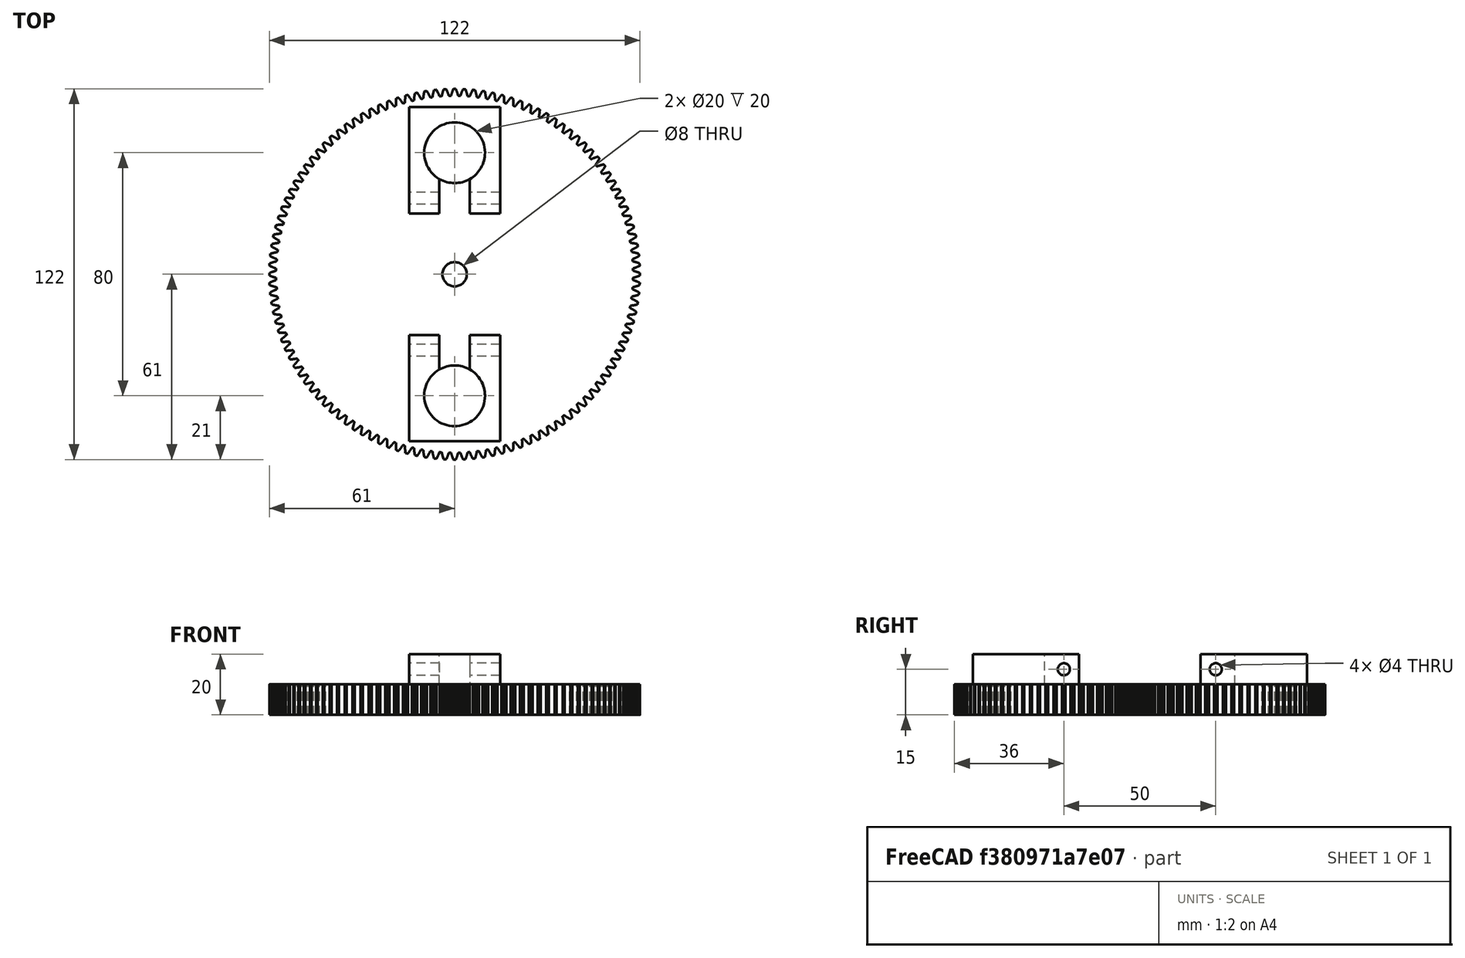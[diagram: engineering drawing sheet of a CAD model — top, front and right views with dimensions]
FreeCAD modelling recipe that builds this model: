
FCSTD DOCUMENT  (FreeCAD 0.17R13522 (Git))
Label: cogwheel-swivel
License: All rights reserved
LicenseURL: http://en.wikipedia.org/wiki/All_rights_reserved
objects: Part::Cylinder×5, Part::Box×3, Part::MultiFuse×2, Part::FeaturePython×1, Part::Cut×1
note: 12 computed .brp shape members not serialized (recipe doc carries the construction recipe); baked Part::Feature solids carry a one-line shape summary decoded from their .brp

FEATURE [Part::FeaturePython] InvoluteGear  # WARN: FeaturePython — macro-defined, semantics opaque (R4)
  backlash = 0
  beta = 0
  clearance = 0.25
  double_helix = false
  head = 0
  height = 10
  module = 1
  numpoints = 6
  pressure_angle = 20
  reversed_backlash = false
  shift = 0
  simple = false
  teeth = 120
  undercut = false
FEATURE [Part::Cylinder] Cylinder
  Angle = 360
  AttacherType = Attacher::AttachEngine3D
  Height = 20
  Placement = pos=(0,-40,0) rot=(0,0,1;0rad)
  Radius = 10
FEATURE [Part::Cylinder] Cylinder001
  Angle = 360
  AttacherType = Attacher::AttachEngine3D
  Height = 20
  Placement = pos=(0,40,0) rot=(0,0,1;0rad)
  Radius = 10
FEATURE [Part::Box] Box  label="Cube"
  AttacherType = Attacher::AttachEngine3D
  Height = 10
  Length = 30
  Placement = pos=(-15,20,10) rot=(0,0,1;0rad)
  Width = 35
FEATURE [Part::Box] Box001  label="Cube001"
  AttacherType = Attacher::AttachEngine3D
  Height = 10
  Length = 30
  Placement = pos=(-15,-55,10) rot=(0,0,1;0rad)
  Width = 35
FEATURE [Part::Cylinder] Cylinder002
  Angle = 360
  AttacherType = Attacher::AttachEngine3D
  Height = 30
  Placement = pos=(15,-25,15) rot=(0,1,0;4.71239rad)
  Radius = 2
FEATURE [Part::Cylinder] Cylinder003
  Angle = 360
  AttacherType = Attacher::AttachEngine3D
  Height = 30
  Placement = pos=(15,25,15) rot=(0,-1,0;1.5708rad)
  Radius = 2
FEATURE [Part::Cylinder] Cylinder004
  Angle = 360
  AttacherType = Attacher::AttachEngine3D
  Height = 10
  Radius = 4
FEATURE [Part::MultiFuse] Fusion  label="Positive Fusion"
  Shapes = -> [Box,InvoluteGear,Box001]
FEATURE [Part::Box] Box002  label="Cube002"
  AttacherType = Attacher::AttachEngine3D
  Height = 10
  Length = 10
  Placement = pos=(-5,-40,10) rot=(0,0,1;0rad)
  Width = 80
FEATURE [Part::MultiFuse] Fusion001  label="Negative Fusion"
  Shapes = -> [Cylinder004,Cylinder003,Cylinder002,Cylinder001,Cylinder,Box002]
FEATURE [Part::Cut] Cut
  Base = -> Fusion
  Tool = -> Fusion001
